# Revit family: BuzziSpace - BuzziShade
name_source: partatom
category: Lighting Fixtures
units: mm (PartAtom-declared; Revit-internal decimal feet)

## family parameters
Always vertical = Yes
Cut with Voids When Loaded = No
Host = Ceiling
Light Source = No
OmniClass Number = 23.80.70.11
OmniClass Title = Luminaries for Internal Lighting
Part Type = Normal
Room Calculation Point = No
Round Connector Dimension = Use Diameter
Shared = No

## types (10) — shared parameters
Diffuser = <By Category>
Glass = <By Category>
Manufacturer = BuzziSpace
Reflector = <By Category>
URL = https://www.buzzi.space

## per-type parameters (varying)
| type | Electrification | Globe | L | M | M + L Cables | Model | Retrofit | Spot | XL | XXL |
| XL- LED Disk | Yes | No | No | No | No | BuzziShade XL - LED Disk | No | No | Yes | No |
| XL - No Electrification | No | No | No | No | No | BuzziShade XL - No Electrification | No | No | Yes | No |
| XXL- LED Disk | Yes | No | No | No | No | BuzziShade XXL - LED Disk | No | No | No | Yes |
| XXL- No Electrification | No | No | No | No | No | BuzziShade XXL - No Electrification | No | No | No | Yes |
| Large - Sol Solo Globe | Yes | Yes | Yes | No | Yes | BuzziShade Large - Sol Solo Globe | No | No | No | No |
| Large - Sol Solo Spot | Yes | No | Yes | No | Yes | BuzziShade Large - Sol Solo Spot | No | Yes | No | No |
| Medium - Sol Solo Globe | Yes | Yes | No | Yes | Yes | BuzziShade Medium - Sol Solo Globe | Yes | No | No | No |
| Medium - Sol Solo Spot | Yes | No | No | Yes | Yes | BuzziShade Medium - Sol Solo Spot | No | Yes | No | No |
| Medium - Retrofit | Yes | No | No | Yes | Yes | BuzziShade Medium - Sol Solo Retrofit | Yes | No | No | No |
| Large- Retrofit | Yes | No | Yes | No | Yes | BuzziShade Large - Sol Solo Retrofit | Yes | No | No | No |

## geometry (parser evidence)
native form markers: Sweep x17
no freeform markers — native parametric forms only
